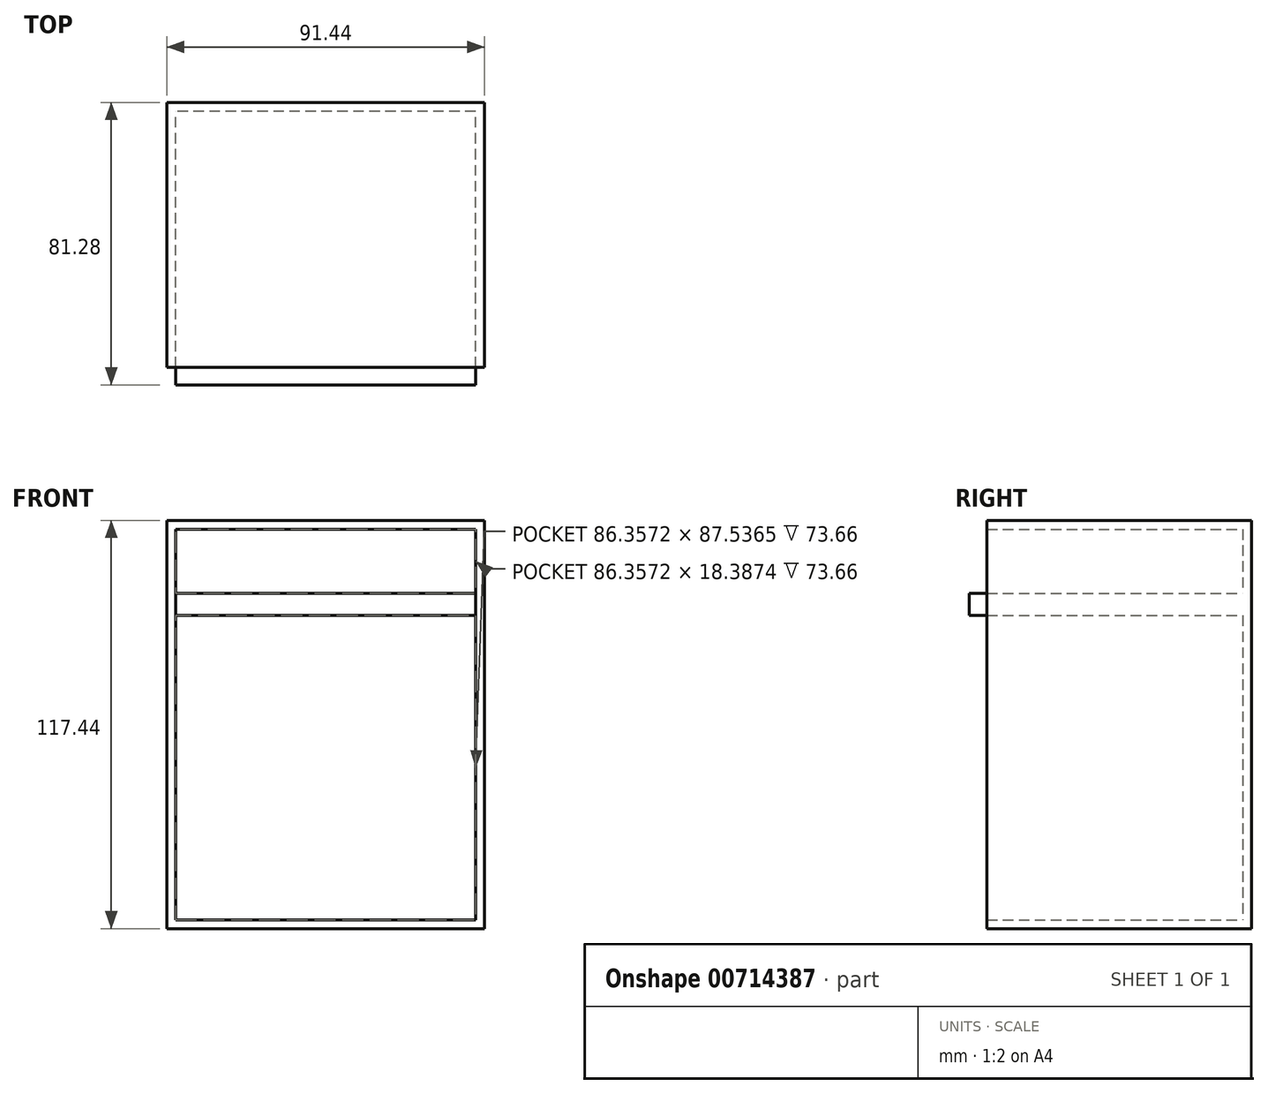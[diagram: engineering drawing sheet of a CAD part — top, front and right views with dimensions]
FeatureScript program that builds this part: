
annotation { "Feature Type Name" : "Feature", "Feature Type Description" : "" }
export const myFeature = defineFeature(function(context is Context, id is Id, definition is map)
    precondition{}
    {
        {
            var Q0;
            Q0=qCreatedBy(makeId("Front.planeOp"),FACE);
            var sketch = newSketch(context, id + "F0", { "sketchPlane" : qUnion([Q0])});
            skLineSegment(sketch, "E0.bottom", {"start": v(-45.72, 53.52) * mm, "end": v(45.72, 53.52) * mm});
            skLineSegment(sketch, "E0.top", {"start": v(-45.72, -63.92) * mm, "end": v(45.72, -63.92) * mm});
            skLineSegment(sketch, "E0.left", {"start": v(-45.72, 53.52) * mm, "end": v(-45.72, -63.92) * mm});
            skLineSegment(sketch, "E0.right", {"start": v(45.72, 53.52) * mm, "end": v(45.72, -63.92) * mm});
            skSolve(sketch);
        }
        {
            var Q0;
            Q0=makeQuery(id+"F0.imprint","IMPRINT",FACE,{"disambiguationData":[TD([[makeQuery(id+"F0.imprint","IMPRINT",EDGE,{"derivedFrom":sQuery(id+"F0.wireOp",EDGE,"E0.bottom")}),-1.0]])]});
            extrude(context, id + "F1", {"entities" : qUnion([Q0]), "depth" : 76.2 * mm, "offsetDistance" : 25.4 * mm});
        }
        {
            var Q0;
            Q0=makeQuery(id+"F1.opExtrude","CAP_FACE",FACE,{"disambiguationData":[OSD([sQuery(id+"F0.wireOp",EDGE,"E0.bottom"),sQuery(id+"F0.wireOp",EDGE,"E0.top"),sQuery(id+"F0.wireOp",EDGE,"E0.left"),sQuery(id+"F0.wireOp",EDGE,"E0.right")])],"isStart":false});
            shell(context, id + "F2", {"entities" : qUnion([Q0]), "thickness" : 2.54 * mm});
        }
        {
            var Q0;
            Q0=makeQuery(id+"F2.opShell","OFFSET_FACE",FACE,{"disambiguationData":[OSD([sQuery(id+"F0.wireOp",EDGE,"E0.bottom"),sQuery(id+"F0.wireOp",EDGE,"E0.top"),sQuery(id+"F0.wireOp",EDGE,"E0.left"),sQuery(id+"F0.wireOp",EDGE,"E0.right")])]});
            var sketch = newSketch(context, id + "F3", { "sketchPlane" : qUnion([Q0])});
            skLineSegment(sketch, "E1.bottom", {"start": v(43.18, 32.6) * mm, "end": v(-43.18, 32.6) * mm});
            skLineSegment(sketch, "E1.top", {"start": v(43.18, 26.16) * mm, "end": v(-43.18, 26.16) * mm});
            skLineSegment(sketch, "E1.left", {"start": v(43.18, 32.6) * mm, "end": v(43.18, 26.16) * mm});
            skLineSegment(sketch, "E1.right", {"start": v(-43.18, 32.6) * mm, "end": v(-43.18, 26.16) * mm});
            skSolve(sketch);
        }
        {
            var Q0;
            Q0 = qSketchRegion(id + "F3", true);
            extrude(context, id + "F4", {"entities" : qUnion([Q0]), "operationType" : NewBodyOperationType.ADD, "depth" : 78.74 * mm, "offsetDistance" : 25.4 * mm});
        }
    });
